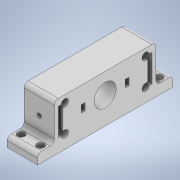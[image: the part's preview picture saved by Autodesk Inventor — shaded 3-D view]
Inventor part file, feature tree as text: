
AUTODESK INVENTOR PART (.ipt)
format: ipt  version: 2020 (Build 240168000, 168)  size: 279,552 bytes
history: native  units: mm
features: extrude x7, sketch x3, other x1, mirror x1, projected_geometry x1
ambient origin geometry x8: Origin, YZ Plane, XZ Plane, XY Plane, X Axis, Y Axis, Z Axis, Center Point
bodies: Body1 (feature_tree)
feature tree (13):
  other  "Bryła1"
  extrude  "Wyciągnięcie proste1"  Depth=33.0mm
  extrude  "Wyciągnięcie proste4"  Depth=10.5mm
  extrude  "Wyciągnięcie proste7"  Depth=40.0mm
  sketch  "Szkic2"
  extrude  "Wyciągnięcie proste5"  Depth=60.0mm
  extrude  "Wyciągnięcie proste6"  Depth=6.0mm
  extrude  "Wyciągnięcie proste9"  Depth=3.5mm
  extrude  "Wyciągnięcie proste10"  TaperAngle=150.0deg  [1 undecoded]
  mirror  "Odbij3"
  sketch  "Szkic3"
  projected_geometry  "Pętla rzutowana1"
  sketch  "Szkic4"
note: 1 required parameter value undecoded (feature->parameter linkage not recoverable at this tier; creation-order binding heuristic only, values carry confidence <= 0.55)
